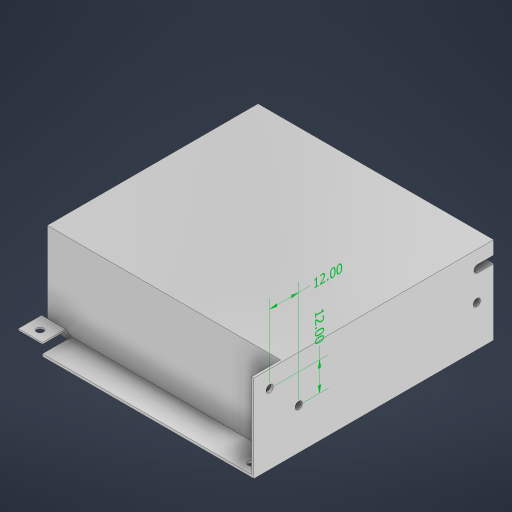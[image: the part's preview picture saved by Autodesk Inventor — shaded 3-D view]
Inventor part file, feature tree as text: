
AUTODESK INVENTOR PART (.ipt)
format: ipt  version: 2024 (Build 280153000, 153)  size: 269,312 bytes
history: native  units: mm
features: extrude x9, sketch x5, other x4, chamfer x2
ambient origin geometry x8: Origin, YZ Plane, XZ Plane, XY Plane, X Axis, Y Axis, Z Axis, Center Point
bodies: Body1 (feature_tree)
feature tree (20):
  other  "솔리드1"
  sketch  "스케치1"
  extrude  "돌출1"  Depth=97.5mm
  extrude  "돌출2"  Depth=99.2mm
  sketch  "스케치2"
  extrude  "돌출3"  Depth=96.5mm
  extrude  "돌출4"  Depth=12.0mm
  extrude  "돌출5"  Depth=1.0mm
  extrude  "돌출6"  Depth=36.0mm TaperAngle=0.0deg
  chamfer  "모따기1"  Distance=1.0mm
  chamfer  "모따기2"  Distance=3.0mm
  sketch  "스케치4"
  extrude  "돌출7"  Depth=5.0mm
  extrude  "돌출8"  Depth=4.0mm
  extrude  "돌출9"  Depth=10.0mm
  sketch  "스케치3"
  sketch  "스케치5"
  other  "선형 치수 1"
  other  "선형 치수 2"
  other  "Finish1"
